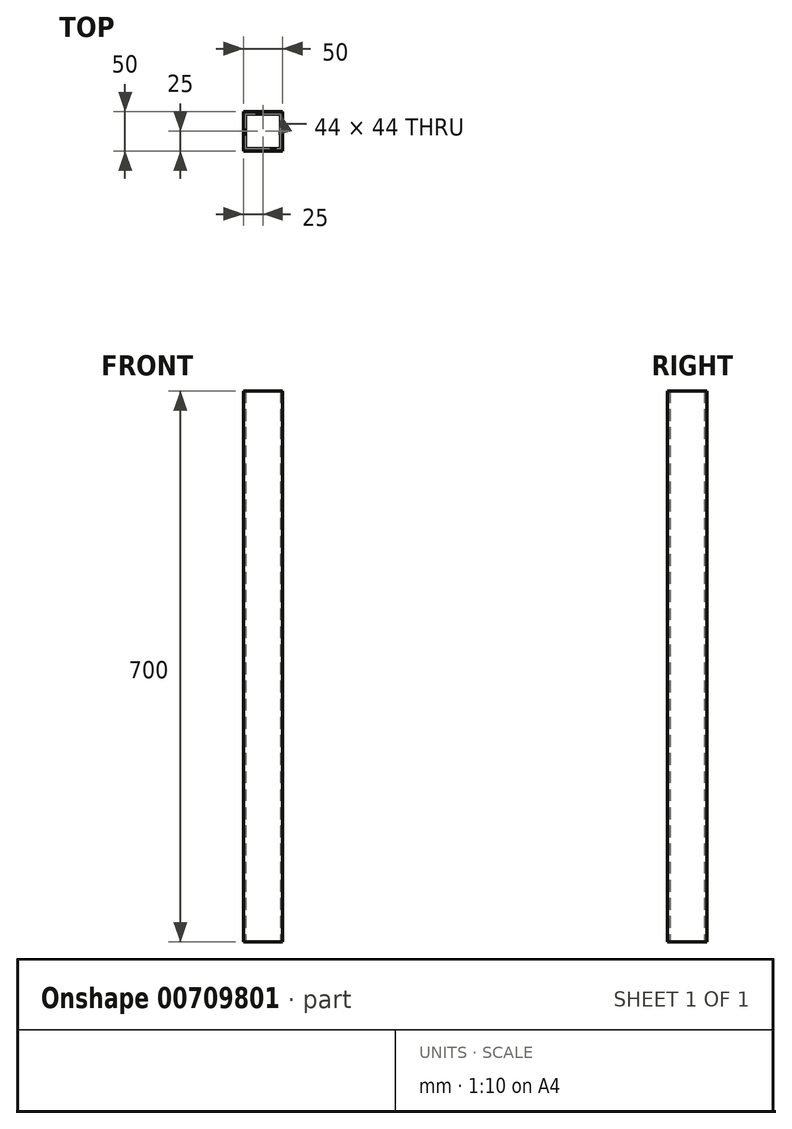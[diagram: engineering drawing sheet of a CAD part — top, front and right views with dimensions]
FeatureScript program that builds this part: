
annotation { "Feature Type Name" : "Feature", "Feature Type Description" : "" }
export const myFeature = defineFeature(function(context is Context, id is Id, definition is map)
    precondition{}
    {
        {
            var Q0;
            Q0=qCreatedBy(makeId("Top.planeOp"),FACE);
            var sketch = newSketch(context, id + "F0", { "sketchPlane" : qUnion([Q0])});
            skLineSegment(sketch, "E0.bottom", {"start": v(0, 0) * mm, "end": v(-50, 0) * mm});
            skLineSegment(sketch, "E0.top", {"start": v(0, 50) * mm, "end": v(-50, 50) * mm});
            skLineSegment(sketch, "E0.left", {"start": v(0, 0) * mm, "end": v(0, 50) * mm});
            skLineSegment(sketch, "E0.right", {"start": v(-50, 0) * mm, "end": v(-50, 50) * mm});
            skLineSegment(sketch, "E1.0", {"start": v(-3, 47) * mm, "end": v(-47, 47) * mm});
            skLineSegment(sketch, "E1.1", {"start": v(-3, 3) * mm, "end": v(-3, 47) * mm});
            skLineSegment(sketch, "E1.2", {"start": v(-3, 3) * mm, "end": v(-47, 3) * mm});
            skLineSegment(sketch, "E1.3", {"start": v(-47, 3) * mm, "end": v(-47, 47) * mm});
            skSolve(sketch);
        }
        {
            var Q0;
            Q0 = qSketchRegion(id + "F0", true);
            extrude(context, id + "F1", {"entities" : qUnion([Q0]), "depth" : 700 * mm, "offsetDistance" : 25 * mm});
        }
    });
